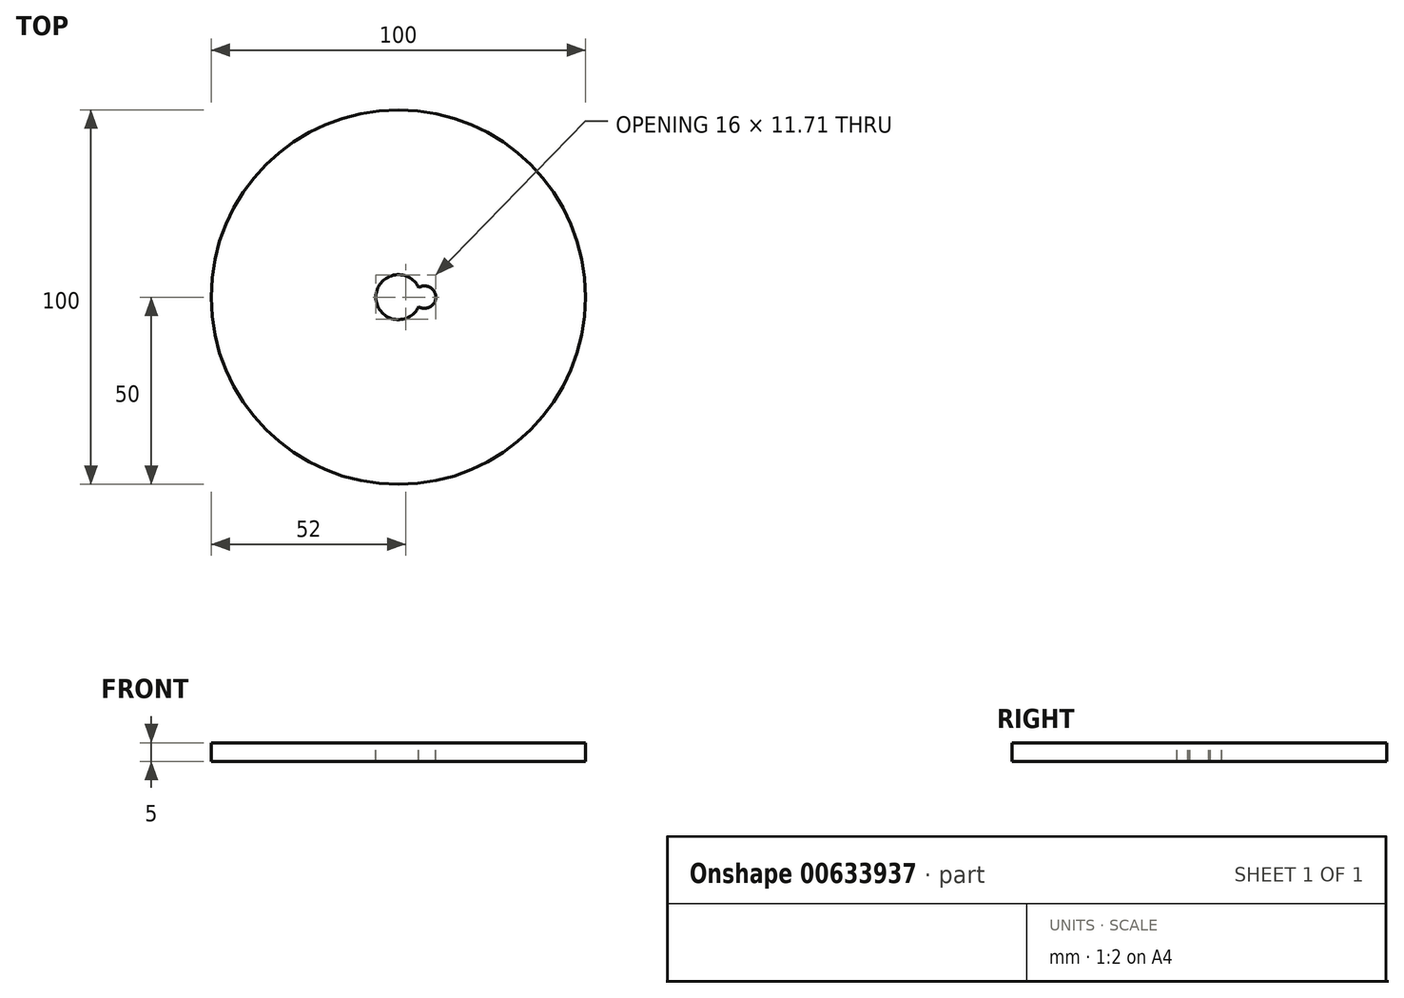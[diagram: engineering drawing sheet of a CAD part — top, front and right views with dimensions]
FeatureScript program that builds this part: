
annotation { "Feature Type Name" : "Feature", "Feature Type Description" : "" }
export const myFeature = defineFeature(function(context is Context, id is Id, definition is map)
    precondition{}
    {
        {
            var Q0;
            Q0=qCreatedBy(makeId("Top.planeOp"),FACE);
            var sketch = newSketch(context, id + "F0", { "sketchPlane" : qUnion([Q0])});
            skCircle(sketch, "E0", {"center": v(0, 0) * mm, "radius": 50 * mm});
            skSolve(sketch);
        }
        {
            var Q0;
            Q0 = qSketchRegion(id + "F0", true);
            extrude(context, id + "F1", {"entities" : qUnion([Q0]), "depth" : 5 * mm, "offsetDistance" : 25 * mm});
        }
        {
            var Q0;
            Q0=makeQuery(id+"F1.opExtrude","CAP_FACE",FACE,{"disambiguationData":[OSD([sQuery(id+"F0.wireOp",EDGE,"E0")])],"isStart":false});
            var sketch = newSketch(context, id + "F2", { "sketchPlane" : qUnion([Q0])});
            skLineSegment(sketch, "E1", {"start": v(-6, 0) * mm, "end": v(0, 0) * mm, "construction": true});
            skArc(sketch, "E2", {"start": v(5.43, 2.56) * mm, "mid": v(-6, 0) * mm, "end": v(5.43, -2.56) * mm});
            skLineSegment(sketch, "E3", {"start": v(0, 0) * mm, "end": v(7, 0) * mm, "construction": true});
            skArc(sketch, "E4", {"start": v(5.43, -2.56) * mm, "mid": v(10, 0) * mm, "end": v(5.43, 2.56) * mm});
            skSolve(sketch);
        }
        {
            var Q0;
            Q0 = qSketchRegion(id + "F2", true);
            extrude(context, id + "F3", {"entities" : qUnion([Q0]), "operationType" : NewBodyOperationType.REMOVE, "endBound" : BoundingType.THROUGH_ALL, "oppositeDirection" : true, "depth" : 25 * mm, "offsetDistance" : 25 * mm});
        }
    });
